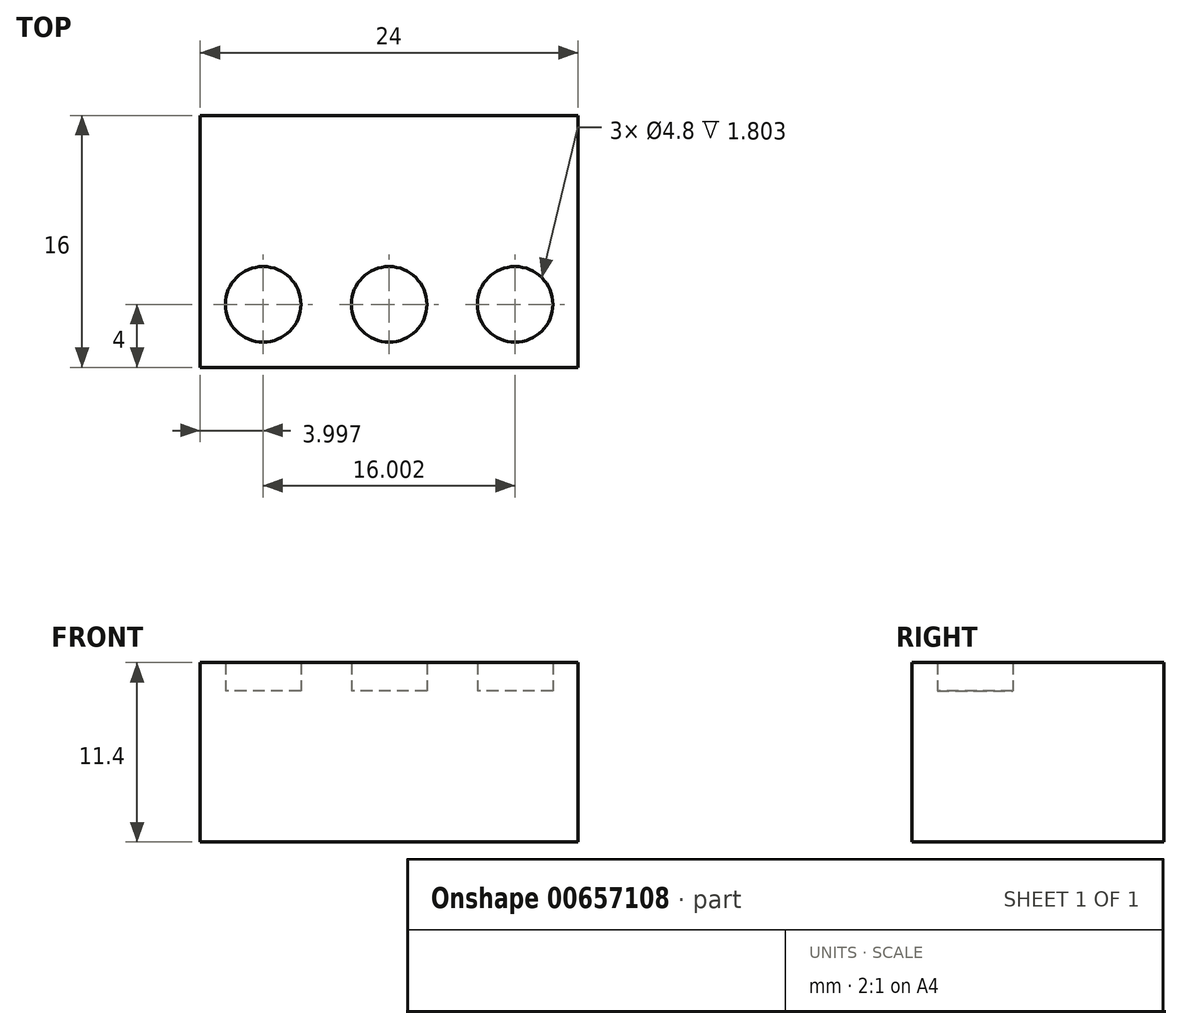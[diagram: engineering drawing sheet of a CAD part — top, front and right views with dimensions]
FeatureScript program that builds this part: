
annotation { "Feature Type Name" : "Feature", "Feature Type Description" : "" }
export const myFeature = defineFeature(function(context is Context, id is Id, definition is map)
    precondition{}
    {
        {
            var Q0;
            Q0=qCreatedBy(makeId("Top.planeOp"),FACE);
            var sketch = newSketch(context, id + "F0", { "sketchPlane" : qUnion([Q0])});
            skLineSegment(sketch, "E0.bottom", {"start": v(0, 0) * mm, "end": v(-24, 0) * mm});
            skLineSegment(sketch, "E0.top", {"start": v(0, 16) * mm, "end": v(-24, 16) * mm});
            skLineSegment(sketch, "E0.left", {"start": v(0, 0) * mm, "end": v(0, 16) * mm});
            skLineSegment(sketch, "E0.right", {"start": v(-24, 0) * mm, "end": v(-24, 16) * mm});
            skSolve(sketch);
        }
        {
            var Q0;
            Q0=makeQuery(id+"F0.imprint","IMPRINT",FACE,{"disambiguationData":[TD([[makeQuery(id+"F0.imprint","IMPRINT",EDGE,{"derivedFrom":sQuery(id+"F0.wireOp",EDGE,"E0.bottom")}),-1.0]])]});
            extrude(context, id + "F1", {"entities" : qUnion([Q0]), "depth" : 9.6 * mm, "offsetDistance" : 25.4 * mm});
        }
        {
            var Q0;
            Q0=makeQuery(id+"F1.opExtrude","CAP_FACE",FACE,{"disambiguationData":[OSD([sQuery(id+"F0.wireOp",EDGE,"E0.bottom"),sQuery(id+"F0.wireOp",EDGE,"E0.top"),sQuery(id+"F0.wireOp",EDGE,"E0.left"),sQuery(id+"F0.wireOp",EDGE,"E0.right")])],"isStart":false});
            var sketch = newSketch(context, id + "F2", { "sketchPlane" : qUnion([Q0])});
            skLineSegment(sketch, "E1", {"start": v(-24, 8) * mm, "end": v(0, 8) * mm, "construction": true});
            skLineSegment(sketch, "E2", {"start": v(-16, 16) * mm, "end": v(-16, 0) * mm, "construction": true});
            skLineSegment(sketch, "E3", {"start": v(-8, 16) * mm, "end": v(-8, 0) * mm, "construction": true});
            skLineSegment(sketch, "E4", {"start": v(-24, 8) * mm, "end": v(-16, 16) * mm, "construction": true});
            skLineSegment(sketch, "E5", {"start": v(-8, 8) * mm, "end": v(-16, 16) * mm, "construction": true});
            skLineSegment(sketch, "E6", {"start": v(-8, 16) * mm, "end": v(0, 8) * mm, "construction": true});
            skCircle(sketch, "E7", {"center": v(-20, 12) * mm, "radius": 2.4 * mm});
            skCircle(sketch, "E8", {"center": v(-12, 12) * mm, "radius": 2.4 * mm});
            skCircle(sketch, "E9", {"center": v(-4, 12) * mm, "radius": 2.4 * mm});
            skLineSegment(sketch, "E10", {"start": v(-24, 8) * mm, "end": v(-16, 0) * mm, "construction": true});
            skLineSegment(sketch, "E11", {"start": v(-8, 8) * mm, "end": v(-16, 0) * mm, "construction": true});
            skLineSegment(sketch, "E12", {"start": v(-8, 8) * mm, "end": v(0, 0) * mm, "construction": true});
            skCircle(sketch, "E13.MirrorC", {"center": v(-20, 4) * mm, "radius": 2.4 * mm});
            skCircle(sketch, "E14.MirrorC", {"center": v(-12, 4) * mm, "radius": 2.4 * mm});
            skCircle(sketch, "E15.MirrorC", {"center": v(-4, 4) * mm, "radius": 2.4 * mm});
            skSolve(sketch);
        }
        {
            var Q0;
            Q0=makeQuery(id+"F2.imprint","IMPRINT",FACE,{"disambiguationData":[TD([[makeQuery(id+"F2.imprint","IMPRINT",EDGE,{"derivedFrom":sQuery(id+"F2.wireOp",EDGE,"E7")}),1.0]])]});
            var Q1;
            Q1=makeQuery(id+"F2.imprint","IMPRINT",FACE,{"disambiguationData":[TD([[makeQuery(id+"F2.imprint","IMPRINT",EDGE,{"derivedFrom":sQuery(id+"F2.wireOp",EDGE,"E8")}),1.0]])]});
            var Q2;
            Q2=makeQuery(id+"F2.imprint","IMPRINT",FACE,{"disambiguationData":[TD([[makeQuery(id+"F2.imprint","IMPRINT",EDGE,{"derivedFrom":sQuery(id+"F2.wireOp",EDGE,"E9")}),1.0]])]});
            var Q3;
            Q3=makeQuery(id+"F2.imprint","IMPRINT",FACE,{"disambiguationData":[TD([[makeQuery(id+"F2.imprint","IMPRINT",EDGE,{"derivedFrom":sQuery(id+"F2.wireOp",EDGE,"E13.MirrorC")}),-1.0]])]});
            var Q4;
            Q4=makeQuery(id+"F2.imprint","IMPRINT",FACE,{"disambiguationData":[TD([[makeQuery(id+"F2.imprint","IMPRINT",EDGE,{"derivedFrom":sQuery(id+"F2.wireOp",EDGE,"E14.MirrorC")}),-1.0]])]});
            var Q5;
            Q5=makeQuery(id+"F2.imprint","IMPRINT",FACE,{"disambiguationData":[TD([[makeQuery(id+"F2.imprint","IMPRINT",EDGE,{"derivedFrom":sQuery(id+"F2.wireOp",EDGE,"E15.MirrorC")}),-1.0]])]});
            extrude(context, id + "F3", {"entities" : qUnion([Q0, Q1, Q2, Q3, Q4, Q5]), "operationType" : NewBodyOperationType.ADD, "depth" : 1.8 * mm, "offsetDistance" : 25.4 * mm});
        }
    });
